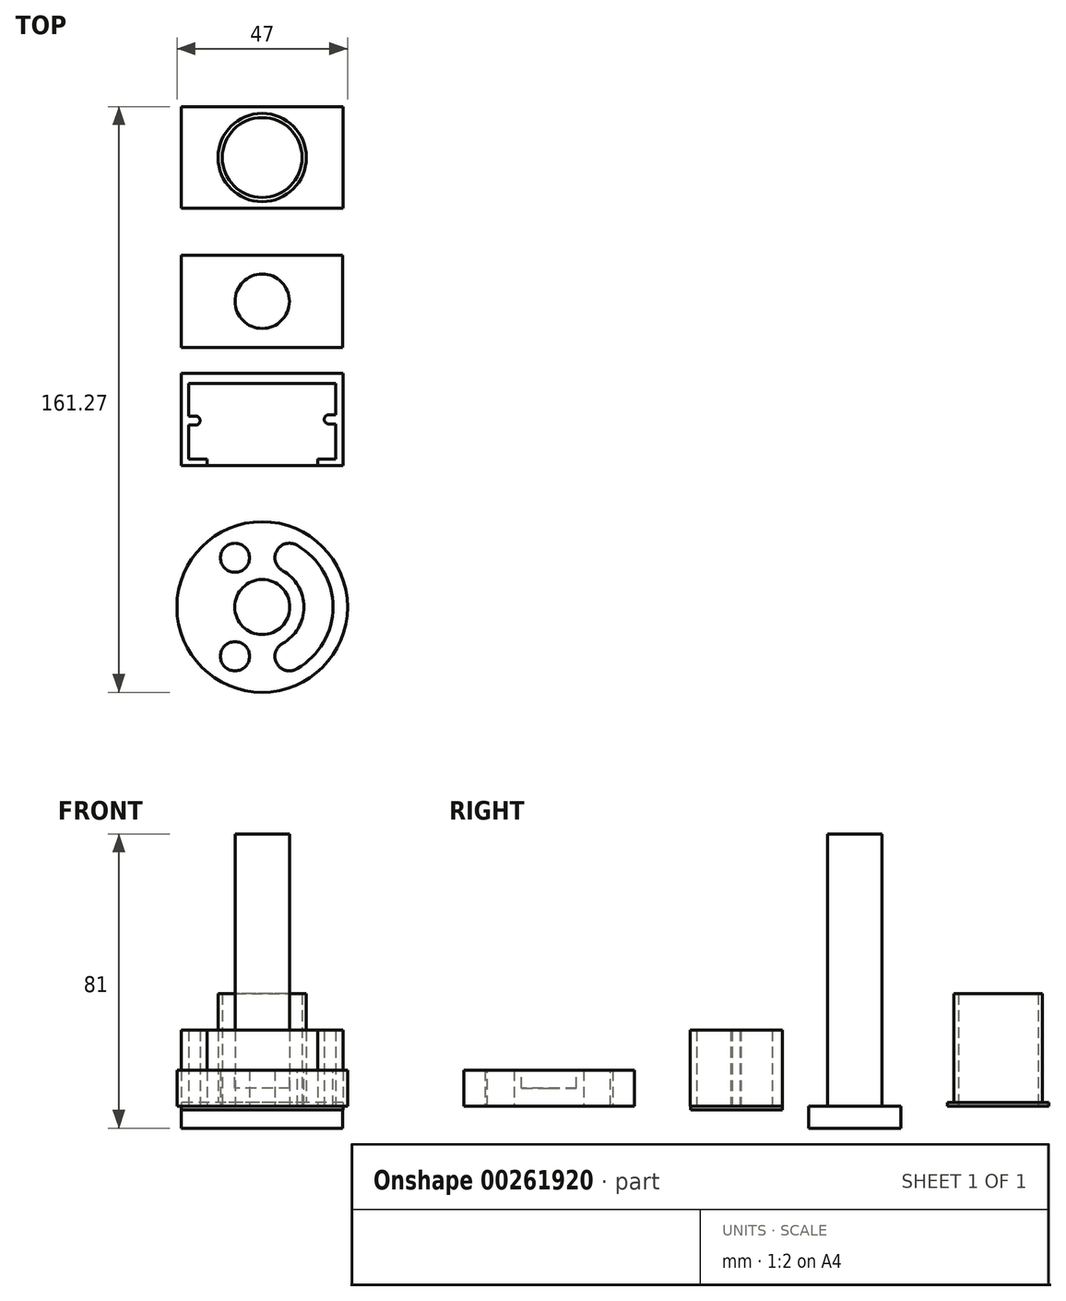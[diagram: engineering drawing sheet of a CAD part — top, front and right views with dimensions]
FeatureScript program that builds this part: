
annotation { "Feature Type Name" : "Feature", "Feature Type Description" : "" }
export const myFeature = defineFeature(function(context is Context, id is Id, definition is map)
    precondition{}
    {
        {
            var Q0;
            Q0=qCreatedBy(makeId("Top.planeOp"),FACE);
            var sketch = newSketch(context, id + "F0", { "sketchPlane" : qUnion([Q0])});
            skLineSegment(sketch, "E0.bottom", {"start": v(22.27, -12.66) * mm, "end": v(-22.27, -12.66) * mm});
            skLineSegment(sketch, "E0.top", {"start": v(22.27, 12.66) * mm, "end": v(-22.27, 12.66) * mm});
            skLineSegment(sketch, "E0.left", {"start": v(22.27, -12.66) * mm, "end": v(22.27, 12.66) * mm});
            skLineSegment(sketch, "E0.right", {"start": v(-22.27, -12.66) * mm, "end": v(-22.27, 12.66) * mm});
            skPoint(sketch, "E0.middle", {"position": v(0, 0) * mm});
            skSolve(sketch);
        }
        {
            var Q0;
            Q0=qCreatedBy(makeId("Top.planeOp"),FACE);
            var sketch = newSketch(context, id + "F1", { "sketchPlane" : qUnion([Q0])});
            skLineSegment(sketch, "E1.top", {"start": v(20.25, 9.9) * mm, "end": v(-19.25, 9.9) * mm});
            skPoint(sketch, "E1.middle", {"position": v(0, 0) * mm});
            skLineSegment(sketch, "E2.top", {"start": v(22.25, 12.7) * mm, "end": v(-22.25, 12.7) * mm});
            skLineSegment(sketch, "E2.left", {"start": v(22.25, -12.7) * mm, "end": v(22.25, 12.7) * mm});
            skLineSegment(sketch, "E2.right", {"start": v(-22.25, -12.7) * mm, "end": v(-22.25, 12.7) * mm});
            skLineSegment(sketch, "E3.bottom", {"start": v(22.2, 19.84) * mm, "end": v(-22.3, 19.84) * mm});
            skLineSegment(sketch, "E3.top", {"start": v(22.2, 45.24) * mm, "end": v(-22.3, 45.24) * mm});
            skLineSegment(sketch, "E3.left", {"start": v(22.2, 19.84) * mm, "end": v(22.2, 45.24) * mm});
            skLineSegment(sketch, "E3.right", {"start": v(-22.3, 19.84) * mm, "end": v(-22.3, 45.24) * mm});
            skLineSegment(sketch, "E4", {"start": v(-15.25, -12.7) * mm, "end": v(-22.25, -12.7) * mm});
            skLineSegment(sketch, "E5", {"start": v(22.25, -12.7) * mm, "end": v(15.25, -12.7) * mm});
            skLineSegment(sketch, "E6", {"start": v(20.25, 9.9) * mm, "end": v(20.25, 1.25) * mm});
            skLineSegment(sketch, "E7", {"start": v(20.25, 1.25) * mm, "end": v(18.35, 1.25) * mm});
            skLineSegment(sketch, "E8", {"start": v(18.35, -1.25) * mm, "end": v(20.25, -1.25) * mm});
            skLineSegment(sketch, "E9", {"start": v(20.25, -1.25) * mm, "end": v(20.25, -9.7) * mm});
            skArc(sketch, "E10", {"start": v(-18.35, 0.92) * mm, "mid": v(-17.1, -0.33) * mm, "end": v(-18.35, -1.58) * mm});
            skArc(sketch, "E11", {"start": v(18.35, 1.25) * mm, "mid": v(17.1, 0) * mm, "end": v(18.35, -1.25) * mm});
            skLineSegment(sketch, "E12", {"start": v(-15.25, -12.7) * mm, "end": v(-15.25, -10.95) * mm});
            skLineSegment(sketch, "E13", {"start": v(15.25, -12.7) * mm, "end": v(15.25, -10.95) * mm});
            skLineSegment(sketch, "E14", {"start": v(-20.25, -10.95) * mm, "end": v(-20.25, -9.7) * mm});
            skLineSegment(sketch, "E15", {"start": v(15.25, -10.95) * mm, "end": v(20.25, -10.95) * mm});
            skLineSegment(sketch, "E16", {"start": v(20.25, -10.95) * mm, "end": v(20.25, -9.7) * mm});
            skLineSegment(sketch, "E17", {"start": v(-20.25, -9.7) * mm, "end": v(-20.25, -1.58) * mm});
            skLineSegment(sketch, "E18", {"start": v(-20.25, 9.9) * mm, "end": v(-20.25, 0.92) * mm});
            skLineSegment(sketch, "E19", {"start": v(-20.25, 9.9) * mm, "end": v(-19.25, 9.9) * mm});
            skLineSegment(sketch, "E20", {"start": v(-20.25, -10.95) * mm, "end": v(-15.25, -10.95) * mm});
            skLineSegment(sketch, "E21", {"start": v(-20.25, 0.92) * mm, "end": v(-18.35, 0.92) * mm});
            skLineSegment(sketch, "E22", {"start": v(-18.35, -1.58) * mm, "end": v(-20.25, -1.58) * mm});
            skSolve(sketch);
        }
        {
            var Q0;
            Q0=makeQuery(id+"F1.imprint","IMPRINT",FACE,{"disambiguationData":[TD([[makeQuery(id+"F1.imprint","IMPRINT",EDGE,{"derivedFrom":sQuery(id+"F1.wireOp",EDGE,"E1.top")}),-1.0]])]});
            extrude(context, id + "F2", {"entities" : qUnion([Q0]), "depth" : 21 * mm});
        }
        {
            var Q0;
            Q0 = qSketchRegion(id + "F0", true);
            extrude(context, id + "F3", {"entities" : qUnion([Q0]), "operationType" : NewBodyOperationType.ADD, "oppositeDirection" : true, "depth" : 1 * mm});
        }
        {
            var Q0;
            Q0=makeQuery(id+"F1.imprint","IMPRINT",FACE,{"disambiguationData":[TD([[makeQuery(id+"F1.imprint","IMPRINT",EDGE,{"derivedFrom":sQuery(id+"F1.wireOp",EDGE,"E3.bottom")}),-1.0]])]});
            extrude(context, id + "F4", {"entities" : qUnion([Q0]), "oppositeDirection" : true, "depth" : 6 * mm});
        }
        {
            var Q0;
            Q0=makeQuery(id+"F4.opExtrude","CAP_FACE",FACE,{"disambiguationData":[OSD([sQuery(id+"F1.wireOp",EDGE,"E3.bottom"),sQuery(id+"F1.wireOp",EDGE,"E3.top"),sQuery(id+"F1.wireOp",EDGE,"E3.left"),sQuery(id+"F1.wireOp",EDGE,"E3.right")])],"isStart":true});
            var sketch = newSketch(context, id + "F5", { "sketchPlane" : qUnion([Q0])});
            skCircle(sketch, "E23", {"center": v(0, 32.54) * mm, "radius": 7.5 * mm});
            skPoint(sketch, "E23.centerSnap0", {"position": v(22.2, 32.54) * mm});
            skSolve(sketch);
        }
        {
            var Q0;
            Q0=makeQuery(id+"F5.imprint","IMPRINT",FACE,{"disambiguationData":[TD([[makeQuery(id+"F5.imprint","IMPRINT",EDGE,{"derivedFrom":sQuery(id+"F5.wireOp",EDGE,"E23")}),1.0]])]});
            extrude(context, id + "F6", {"entities" : qUnion([Q0]), "operationType" : NewBodyOperationType.ADD, "depth" : 75 * mm});
        }
        {
            var Q0;
            Q0=qCreatedBy(makeId("Top.planeOp"),FACE);
            var sketch = newSketch(context, id + "F7", { "sketchPlane" : qUnion([Q0])});
            skCircle(sketch, "E24", {"center": v(0, -51.66) * mm, "radius": 23.5 * mm});
            skSolve(sketch);
        }
        {
            var Q0;
            Q0 = qSketchRegion(id + "F7", true);
            extrude(context, id + "F8", {"entities" : qUnion([Q0]), "depth" : 10 * mm});
        }
        {
            var Q0;
            Q0=makeQuery(id+"F8.opExtrude","CAP_FACE",FACE,{"disambiguationData":[OSD([sQuery(id+"F7.wireOp",EDGE,"E24")])],"isStart":true});
            var sketch = newSketch(context, id + "F9", { "sketchPlane" : qUnion([Q0])});
            skPoint(sketch, "E25", {"position": v(7.5, 38.1) * mm});
            skPoint(sketch, "E26", {"position": v(-7.5, 38.1) * mm});
            skPoint(sketch, "E27", {"position": v(7.5, 65.23) * mm});
            skPoint(sketch, "E28", {"position": v(-7.5, 65.23) * mm});
            skSolve(sketch);
        }
        {
            var Q0;
            Q0=sQuery(id+"F9.wireOp",VERTEX,"E26");
            var Q1;
            Q1=sQuery(id+"F9.wireOp",VERTEX,"E25");
            var Q2;
            Q2=sQuery(id+"F9.wireOp",VERTEX,"E28");
            var Q3;
            Q3=sQuery(id+"F9.wireOp",VERTEX,"E27");
            var Q4;
            Q4=makeQuery(id+"F8.opExtrude","SWEPT_BODY",BODY,{"disambiguationData":[OSD([sQuery(id+"F7.wireOp",EDGE,"E24")])]});
            hole(context, id + "F10", {"style" : HoleStyle.SIMPLE, "endStyle" : HoleEndStyle.THROUGH, "holeDiameter" : 8 * mm, "tappedDepth" : 12 * mm, "tapClearance" : 3, "locations" : qUnion([Q0, Q1, Q2, Q3]), "scope" : qUnion([Q4])});
        }
        {
            var Q0;
            Q0=makeQuery(id+"F8.opExtrude","CAP_FACE",FACE,{"disambiguationData":[OSD([sQuery(id+"F7.wireOp",EDGE,"E24")])],"isStart":false});
            var sketch = newSketch(context, id + "F11", { "sketchPlane" : qUnion([Q0])});
            skArc(sketch, "E29", {"start": v(9.65, -68.6) * mm, "mid": v(19.5, -51.66) * mm, "end": v(9.65, -34.73) * mm});
            skArc(sketch, "E30", {"start": v(5.55, -41.6) * mm, "mid": v(11.5, -51.65) * mm, "end": v(5.58, -61.72) * mm});
            skArc(sketch, "E31", {"start": v(-5.17, -61.98) * mm, "mid": v(-11.54, -51.66) * mm, "end": v(-5.17, -41.35) * mm});
            skArc(sketch, "E32", {"start": v(-9.55, -68.66) * mm, "mid": v(-19.5, -51.53) * mm, "end": v(-9.32, -34.54) * mm});
            skSolve(sketch);
        }
        {
            var Q0;
            {var subQ0=sQuery(id+"F11.wireOp",EDGE,"E31");var subQ1=makeQuery(id+"F8.opExtrude","CAP_FACE",FACE,{"disambiguationData":[OSD([sQuery(id+"F7.wireOp",EDGE,"E24")])],"isStart":false});var subQ2=makeQuery(id+"F10.hole-2.boolean.opBoolean","INTERSECT",EDGE,{"derivedFrom":[subQ1,makeQuery(id+"F10.hole-2.opRevolve","SWEPT_FACE",FACE,{"disambiguationData":[OSD([sQuery(id+"F10.hole-2.sketch.wireOp",EDGE,"core_line_2")])]})]});var subQ3=makeQuery(id+"F11.imprint","INTERSECT",VERTEX,{"disambiguationData":[OD(1.0)],"derivedFrom":[subQ2,subQ0]});Q0=makeQuery(id+"F11.imprint","IMPRINT",FACE,{"disambiguationData":[TD([[makeQuery(id+"F11.imprint","IMPRINT",EDGE,{"disambiguationData":[TD([[subQ3,-1.0]])],"derivedFrom":subQ0}),1.0]])]});}
            var Q1;
            {var subQ0=sQuery(id+"F11.wireOp",EDGE,"E29");Q1=makeQuery(id+"F11.imprint","IMPRINT",FACE,{"disambiguationData":[TD([[makeQuery(id+"F11.imprint","IMPRINT",EDGE,{"derivedFrom":subQ0}),1.0]])]});}
            extrude(context, id + "F12", {"entities" : qUnion([Q0, Q1]), "operationType" : NewBodyOperationType.REMOVE, "oppositeDirection" : true, "depth" : 25 * mm});
        }
        {
            var Q0;
            Q0=qCreatedBy(makeId("Top.planeOp"),FACE);
            var sketch = newSketch(context, id + "F13", { "sketchPlane" : qUnion([Q0])});
            skLineSegment(sketch, "E33.bottom", {"start": v(22.27, 58.1) * mm, "end": v(-22.27, 58.1) * mm});
            skLineSegment(sketch, "E33.top", {"start": v(22.27, 86.1) * mm, "end": v(-22.27, 86.1) * mm});
            skLineSegment(sketch, "E33.left", {"start": v(22.27, 58.1) * mm, "end": v(22.27, 86.1) * mm});
            skLineSegment(sketch, "E33.right", {"start": v(-22.27, 58.1) * mm, "end": v(-22.27, 86.1) * mm});
            skPoint(sketch, "E33.middle", {"position": v(0, 72.1) * mm});
            skCircle(sketch, "E34", {"center": v(0, 72.1) * mm, "radius": 11 * mm});
            skSolve(sketch);
        }
        {
            var Q0;
            Q0=makeQuery(id+"F13.imprint","IMPRINT",FACE,{"disambiguationData":[TD([[makeQuery(id+"F13.imprint","IMPRINT",EDGE,{"derivedFrom":sQuery(id+"F13.wireOp",EDGE,"E33.bottom")}),-1.0]])]});
            extrude(context, id + "F14", {"entities" : qUnion([Q0]), "depth" : 1 * mm});
        }
        {
            var Q0;
            Q0=makeQuery(id+"F14.opExtrude","CAP_FACE",FACE,{"disambiguationData":[OSD([sQuery(id+"F13.wireOp",EDGE,"E33.bottom"),sQuery(id+"F13.wireOp",EDGE,"E33.top"),sQuery(id+"F13.wireOp",EDGE,"E33.left"),sQuery(id+"F13.wireOp",EDGE,"E33.right"),sQuery(id+"F13.wireOp",EDGE,"E34")])],"isStart":false});
            var sketch = newSketch(context, id + "F15", { "sketchPlane" : qUnion([Q0])});
            skCircle(sketch, "E35", {"center": v(0, 72.1) * mm, "radius": 12.16 * mm});
            skCircle(sketch, "E36", {"center": v(0, 72.1) * mm, "radius": 11 * mm});
            skSolve(sketch);
        }
        {
            var Q0;
            Q0=makeQuery(id+"F15.imprint","IMPRINT",FACE,{"disambiguationData":[TD([[makeQuery(id+"F15.imprint","IMPRINT",EDGE,{"derivedFrom":sQuery(id+"F15.wireOp",EDGE,"E35")}),1.0]])]});
            extrude(context, id + "F16", {"entities" : qUnion([Q0]), "operationType" : NewBodyOperationType.ADD, "depth" : 30 * mm, "offsetDistance" : 25 * mm});
        }
        {
            var Q0;
            Q0=makeQuery(id+"F8.opExtrude","CAP_FACE",FACE,{"disambiguationData":[OSD([sQuery(id+"F7.wireOp",EDGE,"E24")])],"isStart":false});
            var sketch = newSketch(context, id + "F17", { "sketchPlane" : qUnion([Q0])});
            skCircle(sketch, "E37", {"center": v(0, -51.66) * mm, "radius": 7.58 * mm});
            skSolve(sketch);
        }
        {
            var Q0;
            Q0 = qSketchRegion(id + "F17", true);
            extrude(context, id + "F18", {"entities" : qUnion([Q0]), "operationType" : NewBodyOperationType.REMOVE, "oppositeDirection" : true, "depth" : 5 * mm, "offsetDistance" : 25 * mm});
        }
    });
